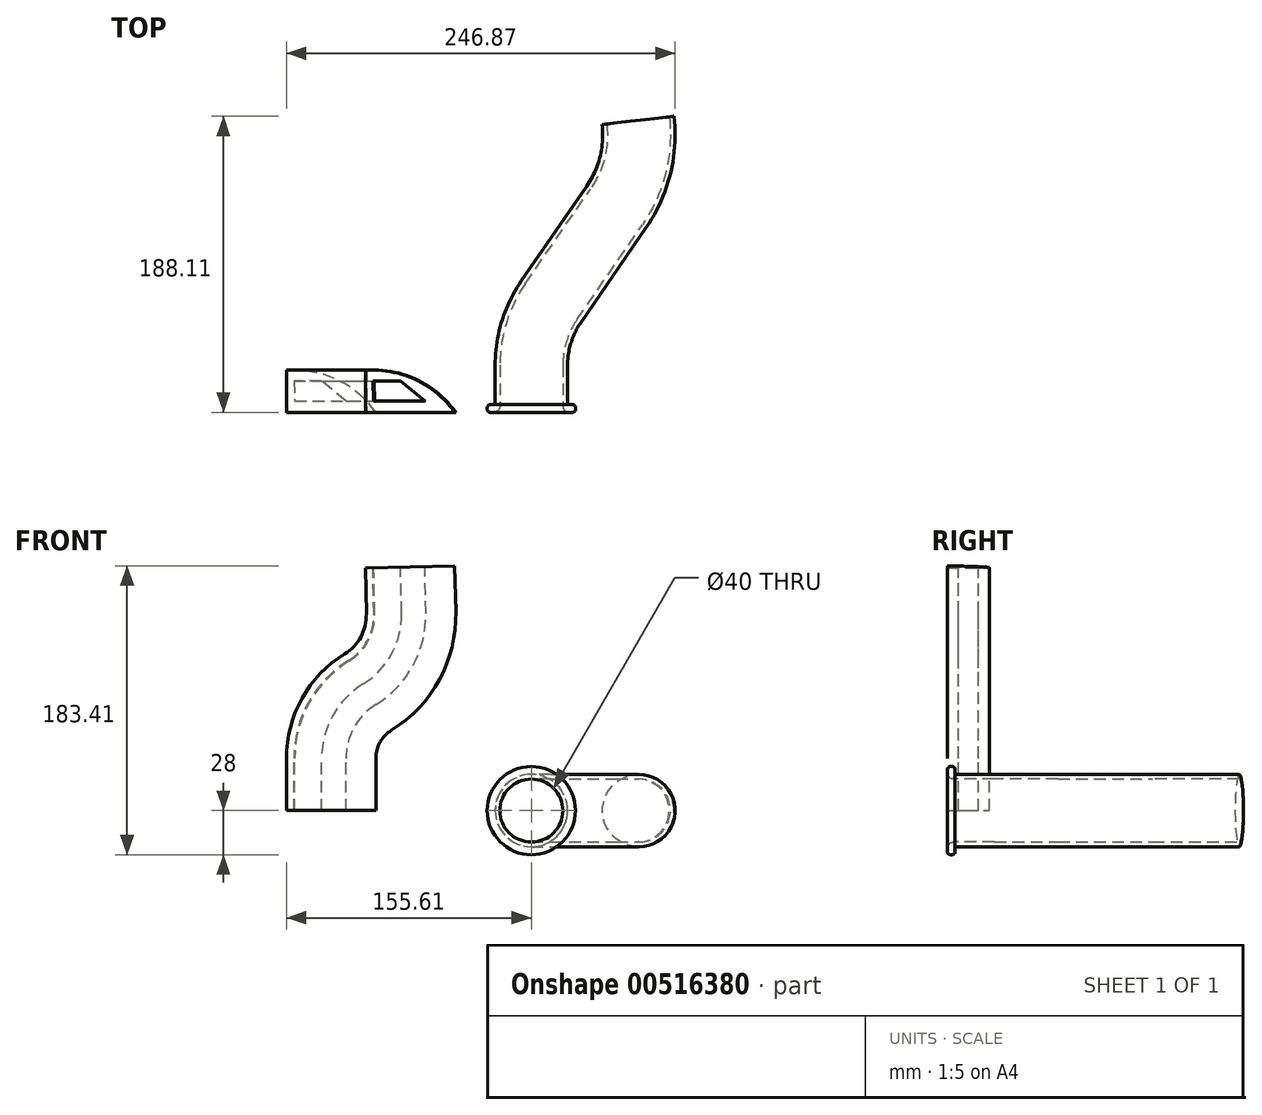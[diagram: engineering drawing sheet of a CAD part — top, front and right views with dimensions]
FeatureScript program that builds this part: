
annotation { "Feature Type Name" : "Feature", "Feature Type Description" : "" }
export const myFeature = defineFeature(function(context is Context, id is Id, definition is map)
    precondition{}
    {
        {
            var Q0;
            Q0=qCreatedBy(makeId("Top.planeOp"),FACE);
            var sketch = newSketch(context, id + "F0", { "sketchPlane" : qUnion([Q0])});
            skLineSegment(sketch, "E0", {"start": v(0, 0) * mm, "end": v(-20, 0) * mm});
            skLineSegment(sketch, "E1", {"start": v(-20, 0) * mm, "end": v(-28, 0) * mm});
            skLineSegment(sketch, "E2", {"start": v(-28, 0) * mm, "end": v(-28, 5) * mm});
            skLineSegment(sketch, "E3", {"start": v(-28, 5) * mm, "end": v(-23, 5) * mm});
            skLineSegment(sketch, "E4", {"start": v(-23, 5) * mm, "end": v(-23, 9) * mm});
            skLineSegment(sketch, "E5", {"start": v(-23, 9) * mm, "end": v(-20, 9) * mm});
            skLineSegment(sketch, "E6", {"start": v(-20, 9) * mm, "end": v(-20, 0) * mm});
            skLineSegment(sketch, "E7", {"start": v(0, 0) * mm, "end": v(0, 30) * mm});
            skArc(sketch, "E8", {"start": v(0, 30) * mm, "mid": v(3.2, 51.08) * mm, "end": v(12.53, 70.25) * mm});
            skLineSegment(sketch, "E9", {"start": v(12.53, 70.25) * mm, "end": v(54.01, 130.44) * mm});
            skArc(sketch, "E10", {"start": v(54.01, 130.44) * mm, "mid": v(65.87, 156.7) * mm, "end": v(67.72, 185.47) * mm});
            skLineSegment(sketch, "E11", {"start": v(-98.78, 0) * mm, "end": v(-155.6, 0) * mm});
            skLineSegment(sketch, "E12", {"start": v(-155.6, 0) * mm, "end": v(-155.6, 26.82) * mm});
            skLineSegment(sketch, "E13", {"start": v(-155.6, 26.82) * mm, "end": v(-150.55, 26.82) * mm});
            skArc(sketch, "E14", {"start": v(-150.55, 26.82) * mm, "mid": v(-121.4, 19.72) * mm, "end": v(-98.78, 0) * mm});
            skLineSegment(sketch, "E15", {"start": v(-150.31, 7.08) * mm, "end": v(-117.8, 7.08) * mm});
            skLineSegment(sketch, "E16", {"start": v(-117.8, 7.08) * mm, "end": v(-133.21, 19.84) * mm});
            skLineSegment(sketch, "E17", {"start": v(-133.21, 19.84) * mm, "end": v(-150.8, 19.84) * mm});
            skLineSegment(sketch, "E18", {"start": v(-150.8, 19.84) * mm, "end": v(-150.31, 7.08) * mm});
            skSolve(sketch);
        }
        {
            var Q0;
            Q0=makeQuery(id+"F0.imprint","IMPRINT",FACE,{"disambiguationData":[TD([[makeQuery(id+"F0.imprint","IMPRINT",EDGE,{"derivedFrom":sQuery(id+"F0.wireOp",EDGE,"E1")}),-1.0]])]});
            var Q1;
            Q1=sQuery(id+"F0.wireOp",EDGE,"E7");
            revolve(context, id + "F1", {"entities" : qUnion([Q0]), "axis" : qUnion([Q1]), "revolveType" : RevolveType.FULL});
        }
        {
            var Q0;
            Q0=makeQuery(id+"F1.opRevolve","SWEPT_FACE",FACE,{"disambiguationData":[OSD([sQuery(id+"F0.wireOp",EDGE,"E5")])]});
            var Q1;
            Q1=sQuery(id+"F0.wireOp",EDGE,"E7");
            var Q2;
            Q2=sQuery(id+"F0.wireOp",EDGE,"E8");
            var Q3;
            Q3=sQuery(id+"F0.wireOp",EDGE,"E9");
            var Q4;
            Q4=sQuery(id+"F0.wireOp",EDGE,"E10");
            sweep(context, id + "F2", {"operationType" : NewBodyOperationType.ADD, "profiles" : qUnion([Q0]), "path" : qUnion([Q1, Q2, Q3, Q4])});
        }
        {
            var Q0;
            Q0=qCreatedBy(makeId("Front.planeOp"),FACE);
            var sketch = newSketch(context, id + "F3", { "sketchPlane" : qUnion([Q0])});
            skLineSegment(sketch, "E19", {"start": v(107, 0) * mm, "end": v(107, 19.54) * mm});
            skArc(sketch, "E20", {"start": v(107, 19.54) * mm, "mid": v(118.62, 61.58) * mm, "end": v(150.15, 91.7) * mm});
            skLineSegment(sketch, "E21", {"start": v(150.15, 91.7) * mm, "end": v(195.9, 116.28) * mm});
            skLineSegment(sketch, "E22", {"start": v(-133.24, 0) * mm, "end": v(-133.24, 33.14) * mm});
            skArc(sketch, "E23", {"start": v(-133.24, 33.14) * mm, "mid": v(-126.18, 60.25) * mm, "end": v(-106.8, 80.48) * mm});
            skArc(sketch, "E24", {"start": v(-106.8, 80.48) * mm, "mid": v(-88.66, 99.63) * mm, "end": v(-82.44, 125.26) * mm});
            skLineSegment(sketch, "E25", {"start": v(-82.44, 125.26) * mm, "end": v(-83.1, 154.65) * mm});
            skSolve(sketch);
        }
        {
            var Q0;
            Q0=makeQuery(id+"F1.opRevolve","SWEPT_EDGE",EDGE,{"disambiguationData":[OSD([sQuery(id+"F0.wireOp",EDGE,"E2"),sQuery(id+"F0.wireOp",EDGE,"E3")])]});
            var Q1;
            Q1=makeQuery(id+"F1.opRevolve","SWEPT_EDGE",EDGE,{"disambiguationData":[OSD([sQuery(id+"F0.wireOp",EDGE,"E1"),sQuery(id+"F0.wireOp",EDGE,"E2")])]});
            fillet(context, id + "F4", {"entities" : qUnion([Q0, Q1]), "radius" : 2 * mm, "tangentPropagation" : true, "allowEdgeOverflow" : false});
        }
        {
            var Q0;
            Q0=makeQuery(id+"F1.opRevolve","SWEPT_EDGE",EDGE,{"disambiguationData":[OSD([sQuery(id+"F0.wireOp",EDGE,"E1"),sQuery(id+"F0.wireOp",EDGE,"E6")])]});
            fillet(context, id + "F5", {"entities" : qUnion([Q0]), "radius" : 4 * mm, "tangentPropagation" : true, "allowEdgeOverflow" : false});
        }
        {
            var Q0;
            Q0=makeQuery(id+"F0.imprint","IMPRINT",FACE,{"disambiguationData":[TD([[makeQuery(id+"F0.imprint","IMPRINT",EDGE,{"derivedFrom":sQuery(id+"F0.wireOp",EDGE,"E11")}),-1.0]])]});
            var Q1;
            Q1=sQuery(id+"F3.wireOp",EDGE,"E22");
            var Q2;
            Q2=sQuery(id+"F3.wireOp",EDGE,"E23");
            var Q3;
            Q3=sQuery(id+"F3.wireOp",EDGE,"E24");
            var Q4;
            Q4=sQuery(id+"F3.wireOp",EDGE,"E25");
            sweep(context, id + "F6", {"profiles" : qUnion([Q0]), "path" : qUnion([Q1, Q2, Q3, Q4])});
        }
    });
